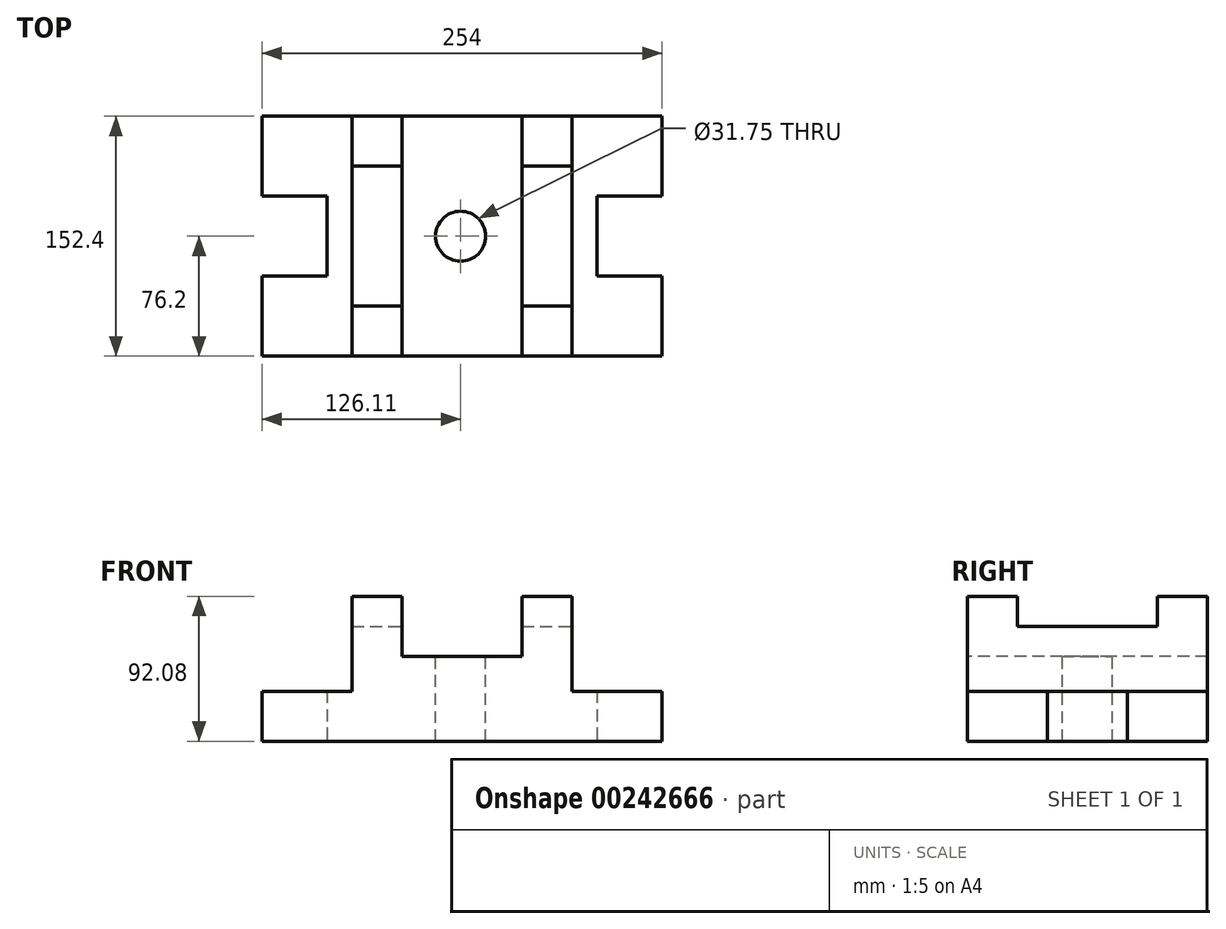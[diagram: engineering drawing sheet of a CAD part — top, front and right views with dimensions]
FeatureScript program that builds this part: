
annotation { "Feature Type Name" : "Feature", "Feature Type Description" : "" }
export const myFeature = defineFeature(function(context is Context, id is Id, definition is map)
    precondition{}
    {
        {
            var Q0;
            Q0=qCreatedBy(makeId("Top.planeOp"),FACE);
            var sketch = newSketch(context, id + "F0", { "sketchPlane" : qUnion([Q0])});
            skLineSegment(sketch, "E0.bottom", {"start": v(-126.1, 76.2) * mm, "end": v(127.9, 76.2) * mm});
            skLineSegment(sketch, "E0.top", {"start": v(-126.1, -76.2) * mm, "end": v(127.9, -76.2) * mm});
            skLineSegment(sketch, "E0.left", {"start": v(-126.1, 76.2) * mm, "end": v(-126.1, -76.2) * mm});
            skLineSegment(sketch, "E0.right", {"start": v(127.9, 76.2) * mm, "end": v(127.9, -76.2) * mm});
            skLineSegment(sketch, "E1", {"start": v(127.9, 25.4) * mm, "end": v(86.62, 25.4) * mm});
            skLineSegment(sketch, "E2.MirrorCS", {"start": v(127.9, -25.4) * mm, "end": v(86.62, -25.4) * mm});
            skLineSegment(sketch, "E3", {"start": v(86.62, 25.4) * mm, "end": v(86.62, -25.4) * mm});
            skLineSegment(sketch, "E4", {"start": v(-126.1, 25.4) * mm, "end": v(-84.83, 25.4) * mm});
            skLineSegment(sketch, "E5.MirrorCS", {"start": v(-126.1, -25.4) * mm, "end": v(-84.83, -25.4) * mm});
            skLineSegment(sketch, "E6", {"start": v(-84.83, 25.4) * mm, "end": v(-84.83, -25.4) * mm});
            skSolve(sketch);
        }
        {
            var Q0;
            {var subQ4=sQuery(id+"F0.wireOp",EDGE,"E0.bottom");Q0=makeQuery(id+"F0.imprint","IMPRINT",FACE,{"disambiguationData":[TD([[makeQuery(id+"F0.imprint","IMPRINT",EDGE,{"derivedFrom":subQ4}),-1.0]])]});}
            extrude(context, id + "F1", {"entities" : qUnion([Q0]), "depth" : 31.75 * mm});
        }
        {
            var Q0;
            Q0=makeQuery(id+"F1.opExtrude","CAP_FACE",FACE,{"disambiguationData":[OSD([sQuery(id+"F0.wireOp",EDGE,"E0.bottom"),sQuery(id+"F0.wireOp",EDGE,"E0.top"),sQuery(id+"F0.wireOp",EDGE,"E0.left"),sQuery(id+"F0.wireOp",EDGE,"E0.right"),sQuery(id+"F0.wireOp",EDGE,"E1"),sQuery(id+"F0.wireOp",EDGE,"E2.MirrorCS"),sQuery(id+"F0.wireOp",EDGE,"E3"),sQuery(id+"F0.wireOp",EDGE,"E4"),sQuery(id+"F0.wireOp",EDGE,"E5.MirrorCS"),sQuery(id+"F0.wireOp",EDGE,"E6")])],"isStart":false});
            var sketch = newSketch(context, id + "F2", { "sketchPlane" : qUnion([Q0])});
            skLineSegment(sketch, "E7", {"start": v(-68.96, 76.2) * mm, "end": v(-68.96, -76.2) * mm});
            skLineSegment(sketch, "E8", {"start": v(-37.2, 76.2) * mm, "end": v(-37.2, -76.2) * mm});
            skLineSegment(sketch, "E9", {"start": v(39, 76.2) * mm, "end": v(39, -76.2) * mm});
            skLineSegment(sketch, "E10", {"start": v(70.74, 76.2) * mm, "end": v(70.74, -76.2) * mm});
            skSolve(sketch);
        }
        {
            var Q0;
            {var subQ0=sQuery(id+"F2.wireOp",EDGE,"E7");Q0=makeQuery(id+"F2.imprint","IMPRINT",FACE,{"disambiguationData":[TD([[makeQuery(id+"F2.imprint","IMPRINT",EDGE,{"derivedFrom":subQ0}),1.0]])]});}
            var Q1;
            {var subQ0=sQuery(id+"F2.wireOp",EDGE,"E8");Q1=makeQuery(id+"F2.imprint","IMPRINT",FACE,{"disambiguationData":[TD([[makeQuery(id+"F2.imprint","IMPRINT",EDGE,{"derivedFrom":subQ0}),1.0]])]});}
            var Q2;
            {var subQ0=sQuery(id+"F2.wireOp",EDGE,"E9");Q2=makeQuery(id+"F2.imprint","IMPRINT",FACE,{"disambiguationData":[TD([[makeQuery(id+"F2.imprint","IMPRINT",EDGE,{"derivedFrom":subQ0}),1.0]])]});}
            extrude(context, id + "F3", {"entities" : qUnion([Q0, Q1, Q2]), "operationType" : NewBodyOperationType.ADD, "depth" : 22.22 * mm});
        }
        {
            var Q0;
            Q0=makeQuery(id+"F3.opExtrude","CAP_FACE",FACE,{"disambiguationData":[OSD([sQuery(id+"F0.wireOp",EDGE,"E0.bottom"),sQuery(id+"F0.wireOp",EDGE,"E0.top"),sQuery(id+"F2.wireOp",EDGE,"E7"),sQuery(id+"F2.wireOp",EDGE,"E10")])],"isStart":false});
            var sketch = newSketch(context, id + "F4", { "sketchPlane" : qUnion([Q0])});
            skLineSegment(sketch, "E11", {"start": v(-37.2, 76.2) * mm, "end": v(-37.2, -76.2) * mm});
            skLineSegment(sketch, "E12", {"start": v(39, 76.2) * mm, "end": v(39, -76.2) * mm});
            skSolve(sketch);
        }
        {
            var Q0;
            {var subQ0=sQuery(id+"F4.wireOp",EDGE,"E11");Q0=makeQuery(id+"F4.imprint","IMPRINT",FACE,{"disambiguationData":[TD([[makeQuery(id+"F4.imprint","IMPRINT",EDGE,{"derivedFrom":subQ0}),-1.0]])]});}
            var Q1;
            {var subQ0=sQuery(id+"F4.wireOp",EDGE,"E12");Q1=makeQuery(id+"F4.imprint","IMPRINT",FACE,{"disambiguationData":[TD([[makeQuery(id+"F4.imprint","IMPRINT",EDGE,{"derivedFrom":subQ0}),1.0]])]});}
            extrude(context, id + "F5", {"entities" : qUnion([Q0, Q1]), "operationType" : NewBodyOperationType.ADD, "depth" : 19.05 * mm});
        }
        {
            var Q0;
            Q0=makeQuery(id+"F5.opExtrude","CAP_FACE",FACE,{"disambiguationData":[OSD([sQuery(id+"F0.wireOp",EDGE,"E0.bottom"),sQuery(id+"F0.wireOp",EDGE,"E0.top"),sQuery(id+"F2.wireOp",EDGE,"E7"),sQuery(id+"F4.wireOp",EDGE,"E11")])],"isStart":false});
            var sketch = newSketch(context, id + "F6", { "sketchPlane" : qUnion([Q0])});
            skLineSegment(sketch, "E13", {"start": v(-68.96, 44.45) * mm, "end": v(-37.2, 44.45) * mm});
            skLineSegment(sketch, "E14", {"start": v(-68.96, -44.45) * mm, "end": v(-37.2, -44.45) * mm});
            skSolve(sketch);
        }
        {
            var Q0;
            {var subQ0=sQuery(id+"F6.wireOp",EDGE,"E13");Q0=makeQuery(id+"F6.imprint","IMPRINT",FACE,{"disambiguationData":[TD([[makeQuery(id+"F6.imprint","IMPRINT",EDGE,{"derivedFrom":subQ0}),1.0]])]});}
            var Q1;
            {var subQ0=sQuery(id+"F6.wireOp",EDGE,"E14");Q1=makeQuery(id+"F6.imprint","IMPRINT",FACE,{"disambiguationData":[TD([[makeQuery(id+"F6.imprint","IMPRINT",EDGE,{"derivedFrom":subQ0}),-1.0]])]});}
            extrude(context, id + "F7", {"entities" : qUnion([Q0, Q1]), "operationType" : NewBodyOperationType.ADD, "depth" : 19.05 * mm});
        }
        {
            var Q0;
            Q0=makeQuery(id+"F5.opExtrude","CAP_FACE",FACE,{"disambiguationData":[OSD([sQuery(id+"F0.wireOp",EDGE,"E0.bottom"),sQuery(id+"F0.wireOp",EDGE,"E0.top"),sQuery(id+"F2.wireOp",EDGE,"E10"),sQuery(id+"F4.wireOp",EDGE,"E12")])],"isStart":false});
            var sketch = newSketch(context, id + "F8", { "sketchPlane" : qUnion([Q0])});
            skLineSegment(sketch, "E15", {"start": v(39, 44.45) * mm, "end": v(70.74, 44.45) * mm});
            skLineSegment(sketch, "E16", {"start": v(39, -44.45) * mm, "end": v(70.74, -44.45) * mm});
            skSolve(sketch);
        }
        {
            var Q0;
            {var subQ0=sQuery(id+"F8.wireOp",EDGE,"E15");Q0=makeQuery(id+"F8.imprint","IMPRINT",FACE,{"disambiguationData":[TD([[makeQuery(id+"F8.imprint","IMPRINT",EDGE,{"derivedFrom":subQ0}),1.0]])]});}
            var Q1;
            {var subQ0=sQuery(id+"F8.wireOp",EDGE,"E16");Q1=makeQuery(id+"F8.imprint","IMPRINT",FACE,{"disambiguationData":[TD([[makeQuery(id+"F8.imprint","IMPRINT",EDGE,{"derivedFrom":subQ0}),-1.0]])]});}
            extrude(context, id + "F9", {"entities" : qUnion([Q0, Q1]), "operationType" : NewBodyOperationType.ADD, "depth" : 19.05 * mm});
        }
        {
            var Q0;
            Q0=makeQuery(id+"F3.opExtrude","CAP_FACE",FACE,{"disambiguationData":[OSD([sQuery(id+"F0.wireOp",EDGE,"E0.bottom"),sQuery(id+"F0.wireOp",EDGE,"E0.top"),sQuery(id+"F2.wireOp",EDGE,"E7"),sQuery(id+"F2.wireOp",EDGE,"E10")])],"isStart":false});
            var sketch = newSketch(context, id + "F10", { "sketchPlane" : qUnion([Q0])});
            skCircle(sketch, "E17", {"center": v(0, 0) * mm, "radius": 15.88 * mm});
            skSolve(sketch);
        }
        {
            var Q0;
            Q0=makeQuery(id+"F10.imprint","IMPRINT",FACE,{"disambiguationData":[TD([[makeQuery(id+"F10.imprint","IMPRINT",EDGE,{"derivedFrom":sQuery(id+"F10.wireOp",EDGE,"E17")}),1.0]])]});
            extrude(context, id + "F11", {"entities" : qUnion([Q0]), "operationType" : NewBodyOperationType.REMOVE, "oppositeDirection" : true, "depth" : 92.07 * mm});
        }
        {
            var Q0;
            Q0=makeQuery(id+"F1.opExtrude","SWEPT_BODY",BODY,{"disambiguationData":[OSD([sQuery(id+"F0.wireOp",EDGE,"E0.bottom"),sQuery(id+"F0.wireOp",EDGE,"E0.top"),sQuery(id+"F0.wireOp",EDGE,"E0.left"),sQuery(id+"F0.wireOp",EDGE,"E0.right"),sQuery(id+"F0.wireOp",EDGE,"E1"),sQuery(id+"F0.wireOp",EDGE,"E2.MirrorCS"),sQuery(id+"F0.wireOp",EDGE,"E3"),sQuery(id+"F0.wireOp",EDGE,"E4"),sQuery(id+"F0.wireOp",EDGE,"E5.MirrorCS"),sQuery(id+"F0.wireOp",EDGE,"E6")])]});
            var Q1;
            Q1=qCreatedBy(makeId("Origin.pointOp"),VERTEX);
            transform(context, id + "F12", {"entities" : qUnion([Q0]), "transformType" : TransformType.SCALE_UNIFORMLY, "scale" : 1, "scalePoint" : qUnion([Q1]), "makeCopy" : false});
        }
    });
